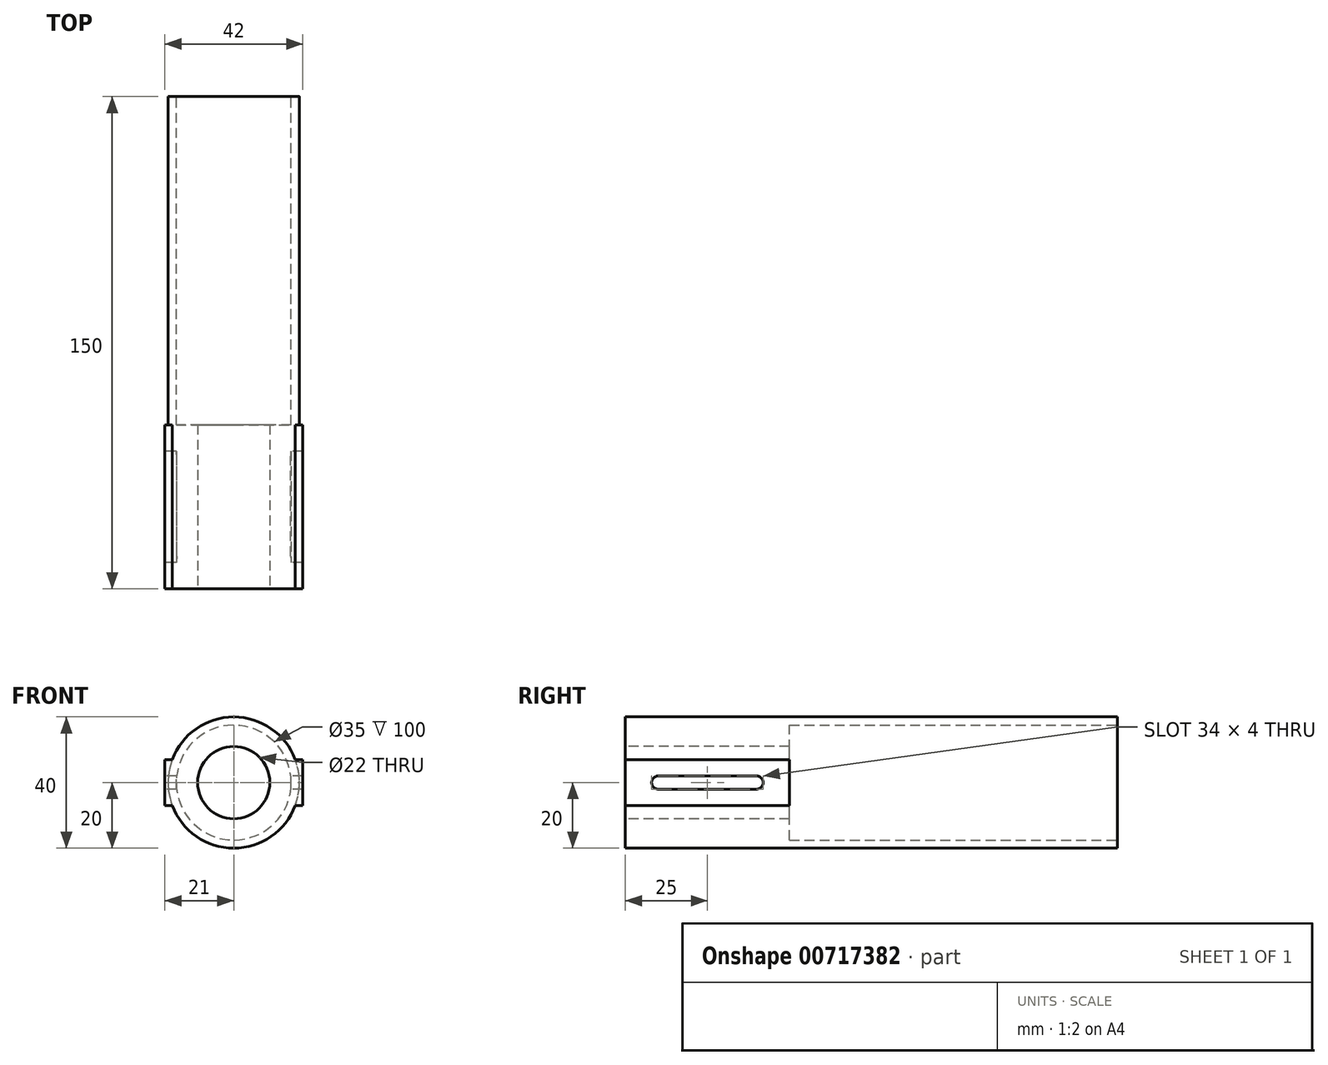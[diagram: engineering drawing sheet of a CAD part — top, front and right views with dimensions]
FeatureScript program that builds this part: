
annotation { "Feature Type Name" : "Feature", "Feature Type Description" : "" }
export const myFeature = defineFeature(function(context is Context, id is Id, definition is map)
    precondition{}
    {
        {
            var Q0;
            Q0=qCreatedBy(makeId("Front.planeOp"),FACE);
            var sketch = newSketch(context, id + "F0", { "sketchPlane" : qUnion([Q0])});
            skCircle(sketch, "E0", {"center": v(0, 0) * mm, "radius": 17.5 * mm});
            skCircle(sketch, "E1", {"center": v(0, 0) * mm, "radius": 20 * mm});
            skSolve(sketch);
        }
        {
            var Q0;
            Q0=makeQuery(id+"F0.imprint","IMPRINT",FACE,{"disambiguationData":[TD([[makeQuery(id+"F0.imprint","IMPRINT",EDGE,{"derivedFrom":sQuery(id+"F0.wireOp",EDGE,"E0")}),-1.0]])]});
            extrude(context, id + "F1", {"entities" : qUnion([Q0]), "depth" : 150 * mm, "offsetDistance" : 25 * mm});
        }
        {
            var Q0;
            Q0=makeQuery(id+"F1.opExtrude","CAP_FACE",FACE,{"disambiguationData":[OSD([sQuery(id+"F0.wireOp",EDGE,"E0"),sQuery(id+"F0.wireOp",EDGE,"E1")])],"isStart":false});
            var sketch = newSketch(context, id + "F2", { "sketchPlane" : qUnion([Q0])});
            skLineSegment(sketch, "E2", {"start": v(-18.73, -7) * mm, "end": v(-21, -7) * mm});
            skLineSegment(sketch, "E3", {"start": v(-21, -7) * mm, "end": v(-21, 7) * mm});
            skLineSegment(sketch, "E4", {"start": v(-21, 7) * mm, "end": v(-18.73, 7) * mm});
            skLineSegment(sketch, "E5", {"start": v(-18.73, 7) * mm, "end": v(-18.73, -7) * mm});
            skLineSegment(sketch, "E6.MirrorCS", {"start": v(18.73, 7) * mm, "end": v(18.73, -7) * mm});
            skLineSegment(sketch, "E7.MirrorCS", {"start": v(21, -7) * mm, "end": v(21, 7) * mm});
            skLineSegment(sketch, "E8.MirrorCS", {"start": v(18.73, -7) * mm, "end": v(21, -7) * mm});
            skLineSegment(sketch, "E9.MirrorCS", {"start": v(21, 7) * mm, "end": v(18.73, 7) * mm});
            skSolve(sketch);
        }
        {
            var Q0;
            Q0 = qSketchRegion(id + "F2", true);
            extrude(context, id + "F3", {"entities" : qUnion([Q0]), "operationType" : NewBodyOperationType.ADD, "oppositeDirection" : true, "depth" : 50 * mm, "offsetDistance" : 25 * mm});
        }
        {
            var Q0;
            Q0=makeQuery(id+"F3.opExtrude","SWEPT_FACE",FACE,{"disambiguationData":[OSD([sQuery(id+"F2.wireOp",EDGE,"E3")])]});
            var sketch = newSketch(context, id + "F4", { "sketchPlane" : qUnion([Q0])});
            skLineSegment(sketch, "E10", {"start": v(110, 0) * mm, "end": v(140, 0) * mm});
            skPoint(sketch, "E10.startSnap0", {"position": v(100, 0) * mm});
            skArc(sketch, "E11.0.startCap", {"start": v(110, -2) * mm, "mid": v(108, 0) * mm, "end": v(110, 2) * mm});
            skArc(sketch, "E11.0.endCap", {"start": v(140, 2) * mm, "mid": v(142, 0) * mm, "end": v(140, -2) * mm});
            skLineSegment(sketch, "E11.0.left", {"start": v(110, 2) * mm, "end": v(140, 2) * mm});
            skLineSegment(sketch, "E11.0.right", {"start": v(110, -2) * mm, "end": v(140, -2) * mm});
            skSolve(sketch);
        }
        {
            var Q0;
            Q0 = qSketchRegion(id + "F4", true);
            extrude(context, id + "F5", {"entities" : qUnion([Q0]), "operationType" : NewBodyOperationType.REMOVE, "endBound" : BoundingType.THROUGH_ALL, "oppositeDirection" : true, "depth" : 25 * mm, "offsetDistance" : 25 * mm});
        }
        {
            var Q0;
            Q0=makeQuery(id+"F3.boolean.opBoolean","MERGE",FACE,{"derivedFrom":[makeQuery(id+"F1.opExtrude","CAP_FACE",FACE,{"disambiguationData":[OSD([sQuery(id+"F0.wireOp",EDGE,"E0"),sQuery(id+"F0.wireOp",EDGE,"E1")])],"isStart":false}),makeQuery(id+"F3.opExtrude","CAP_FACE",FACE,{"disambiguationData":[OSD([sQuery(id+"F2.wireOp",EDGE,"E2"),sQuery(id+"F2.wireOp",EDGE,"E3"),sQuery(id+"F2.wireOp",EDGE,"E4"),sQuery(id+"F2.wireOp",EDGE,"E5")])],"isStart":true}),makeQuery(id+"F3.opExtrude","CAP_FACE",FACE,{"disambiguationData":[OSD([sQuery(id+"F2.wireOp",EDGE,"E6.MirrorCS"),sQuery(id+"F2.wireOp",EDGE,"E7.MirrorCS"),sQuery(id+"F2.wireOp",EDGE,"E8.MirrorCS"),sQuery(id+"F2.wireOp",EDGE,"E9.MirrorCS")])],"isStart":true})]});
            var sketch = newSketch(context, id + "F6", { "sketchPlane" : qUnion([Q0])});
            skCircle(sketch, "E12.0", {"center": v(0, 0) * mm, "radius": 17.5 * mm});
            skCircle(sketch, "E13", {"center": v(0, 0) * mm, "radius": 11 * mm});
            skSolve(sketch);
        }
        {
            var Q0;
            Q0 = qSketchRegion(id + "F6", true);
            extrude(context, id + "F7", {"entities" : qUnion([Q0]), "operationType" : NewBodyOperationType.ADD, "oppositeDirection" : true, "depth" : 50 * mm, "offsetDistance" : 25 * mm});
        }
    });
